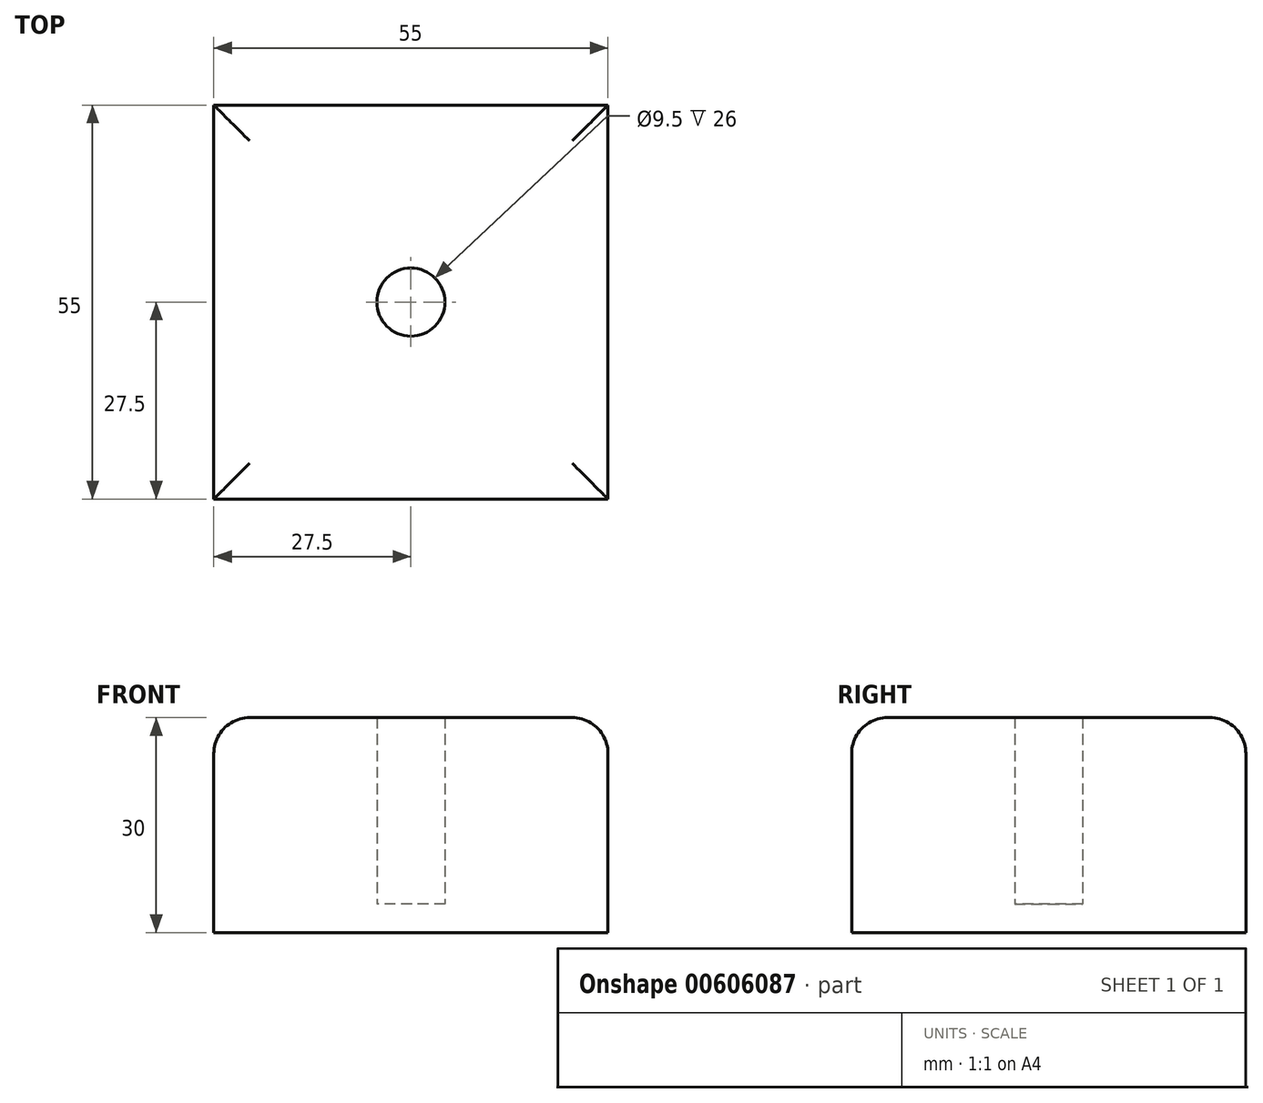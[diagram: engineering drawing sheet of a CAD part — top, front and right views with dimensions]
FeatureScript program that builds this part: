
annotation { "Feature Type Name" : "Feature", "Feature Type Description" : "" }
export const myFeature = defineFeature(function(context is Context, id is Id, definition is map)
    precondition{}
    {
        {
            var Q0;
            Q0=qCreatedBy(makeId("Top.planeOp"),FACE);
            var sketch = newSketch(context, id + "F0", { "sketchPlane" : qUnion([Q0])});
            skLineSegment(sketch, "E0.bottom", {"start": v(27.5, 27.5) * mm, "end": v(-27.5, 27.5) * mm});
            skLineSegment(sketch, "E0.top", {"start": v(27.5, -27.5) * mm, "end": v(-27.5, -27.5) * mm});
            skLineSegment(sketch, "E0.left", {"start": v(27.5, 27.5) * mm, "end": v(27.5, -27.5) * mm});
            skLineSegment(sketch, "E0.right", {"start": v(-27.5, 27.5) * mm, "end": v(-27.5, -27.5) * mm});
            skPoint(sketch, "E0.middle", {"position": v(0, 0) * mm});
            skSolve(sketch);
        }
        {
            var Q0;
            Q0=makeQuery(id+"F0.imprint","IMPRINT",FACE,{"disambiguationData":[TD([[makeQuery(id+"F0.imprint","IMPRINT",EDGE,{"derivedFrom":sQuery(id+"F0.wireOp",EDGE,"E0.bottom")}),1.0]])]});
            extrude(context, id + "F1", {"entities" : qUnion([Q0]), "depth" : 4 * mm, "offsetDistance" : 25 * mm});
        }
        {
            var Q0;
            Q0=makeQuery(id+"F1.opExtrude","CAP_FACE",FACE,{"disambiguationData":[OSD([sQuery(id+"F0.wireOp",EDGE,"E0.bottom"),sQuery(id+"F0.wireOp",EDGE,"E0.top"),sQuery(id+"F0.wireOp",EDGE,"E0.left"),sQuery(id+"F0.wireOp",EDGE,"E0.right")])],"isStart":false});
            var sketch = newSketch(context, id + "F2", { "sketchPlane" : qUnion([Q0])});
            skCircle(sketch, "E1", {"center": v(0, 0) * mm, "radius": 4.75 * mm});
            skSolve(sketch);
        }
        {
            var Q0;
            Q0=makeQuery(id+"F2.imprint","IMPRINT",FACE,{"disambiguationData":[TD([[makeQuery(id+"F2.imprint","IMPRINT",EDGE,{"derivedFrom":sQuery(id+"F2.wireOp",EDGE,"E1")}),-1.0]])]});
            extrude(context, id + "F3", {"entities" : qUnion([Q0]), "operationType" : NewBodyOperationType.ADD, "depth" : 26 * mm, "offsetDistance" : 25 * mm});
        }
        {
            var Q0;
            Q0=makeQuery(id+"F3.opExtrude","CAP_EDGE",EDGE,{"disambiguationData":[OSD([sQuery(id+"F0.wireOp",EDGE,"E0.bottom")])],"isStart":false});
            var Q1;
            Q1=makeQuery(id+"F3.opExtrude","CAP_EDGE",EDGE,{"disambiguationData":[OSD([sQuery(id+"F0.wireOp",EDGE,"E0.right")])],"isStart":false});
            var Q2;
            Q2=makeQuery(id+"F3.opExtrude","CAP_EDGE",EDGE,{"disambiguationData":[OSD([sQuery(id+"F0.wireOp",EDGE,"E0.top")])],"isStart":false});
            var Q3;
            Q3=makeQuery(id+"F3.opExtrude","CAP_EDGE",EDGE,{"disambiguationData":[OSD([sQuery(id+"F0.wireOp",EDGE,"E0.left")])],"isStart":false});
            fillet(context, id + "F4", {"entities" : qUnion([Q0, Q1, Q2, Q3]), "radius" : 5 * mm, "tangentPropagation" : true, "allowEdgeOverflow" : false});
        }
    });
